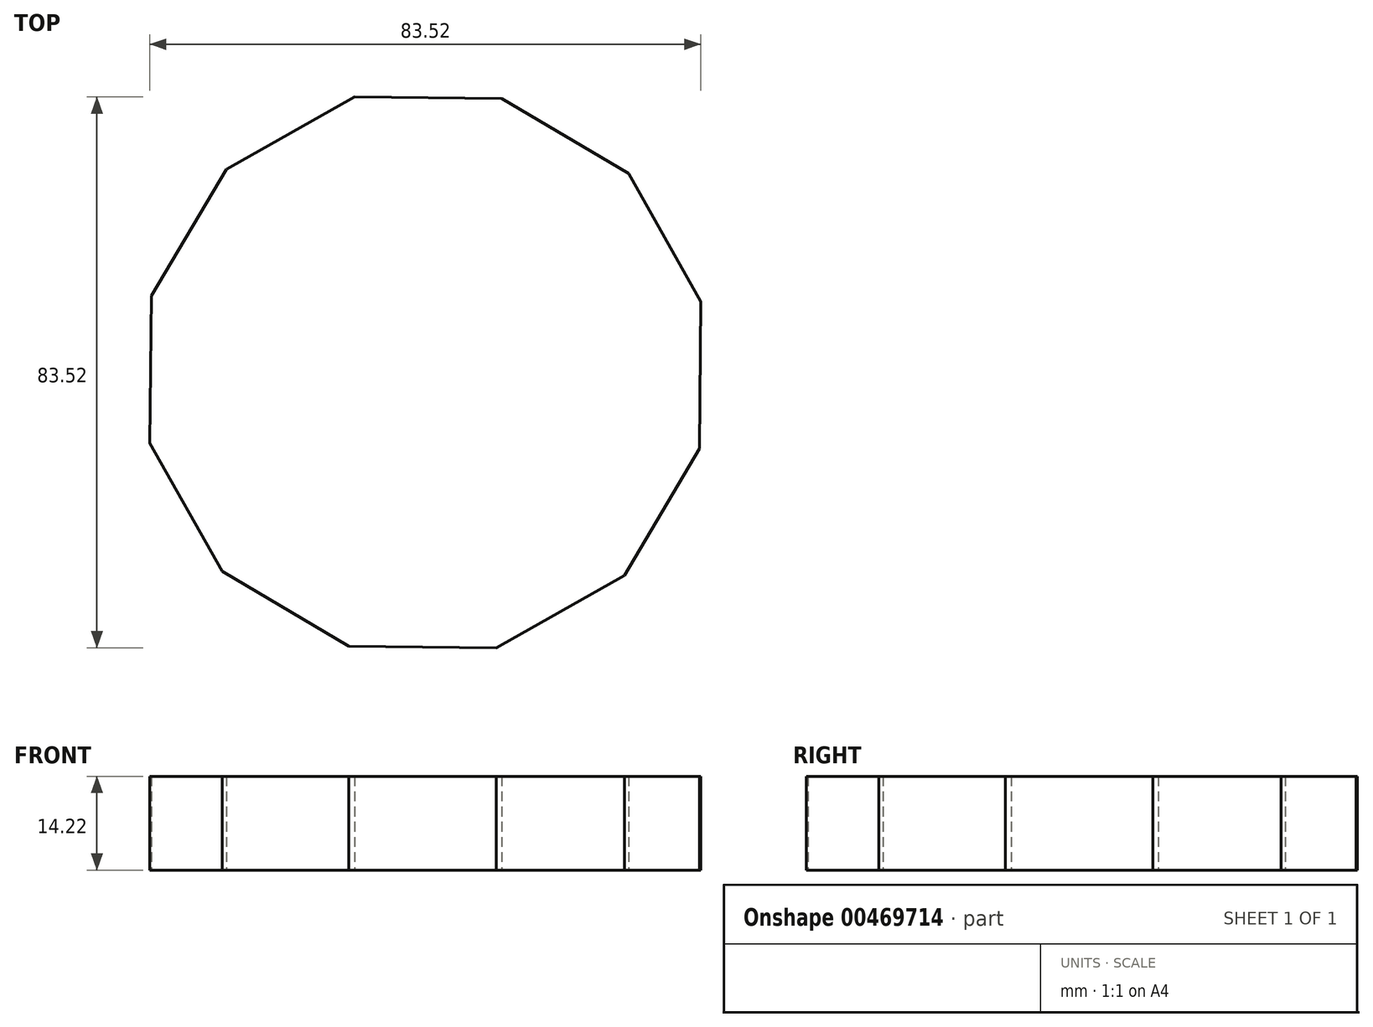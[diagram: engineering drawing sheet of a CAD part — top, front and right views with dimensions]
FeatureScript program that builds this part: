
annotation { "Feature Type Name" : "Feature", "Feature Type Description" : "" }
export const myFeature = defineFeature(function(context is Context, id is Id, definition is map)
    precondition{}
    {
        {
            var Q0;
            Q0=qCreatedBy(makeId("Top.planeOp"),FACE);
            var sketch = newSketch(context, id + "F0", { "sketchPlane" : qUnion([Q0])});
            skCircle(sketch, "E0.cCircle", {"center": v(0, 0) * mm, "radius": 41.64 * mm, "construction": true});
            skLineSegment(sketch, "E0.0", {"start": v(-41.53, 11.59) * mm, "end": v(-30.17, 30.8) * mm});
            skLineSegment(sketch, "E0.1", {"start": v(-30.17, 30.8) * mm, "end": v(-10.73, 41.76) * mm});
            skLineSegment(sketch, "E0.2", {"start": v(-10.73, 41.76) * mm, "end": v(11.59, 41.53) * mm});
            skLineSegment(sketch, "E0.3", {"start": v(11.59, 41.53) * mm, "end": v(30.8, 30.17) * mm});
            skLineSegment(sketch, "E0.4", {"start": v(30.8, 30.17) * mm, "end": v(41.76, 10.73) * mm});
            skLineSegment(sketch, "E0.5", {"start": v(41.76, 10.73) * mm, "end": v(41.53, -11.59) * mm});
            skLineSegment(sketch, "E0.6", {"start": v(41.53, -11.59) * mm, "end": v(30.17, -30.8) * mm});
            skLineSegment(sketch, "E0.7", {"start": v(30.17, -30.8) * mm, "end": v(10.73, -41.76) * mm});
            skLineSegment(sketch, "E0.8", {"start": v(10.73, -41.76) * mm, "end": v(-11.59, -41.53) * mm});
            skLineSegment(sketch, "E0.9", {"start": v(-11.59, -41.53) * mm, "end": v(-30.8, -30.17) * mm});
            skLineSegment(sketch, "E0.10", {"start": v(-30.8, -30.17) * mm, "end": v(-41.76, -10.73) * mm});
            skLineSegment(sketch, "E0.11", {"start": v(-41.76, -10.73) * mm, "end": v(-41.53, 11.59) * mm});
            skPoint(sketch, "E0.0.midPoint", {"position": v(-35.85, 21.2) * mm});
            skSolve(sketch);
        }
        {
            var Q0;
            Q0 = qSketchRegion(id + "F0", true);
            extrude(context, id + "F1", {"entities" : qUnion([Q0]), "depth" : 14.22 * mm});
        }
    });
